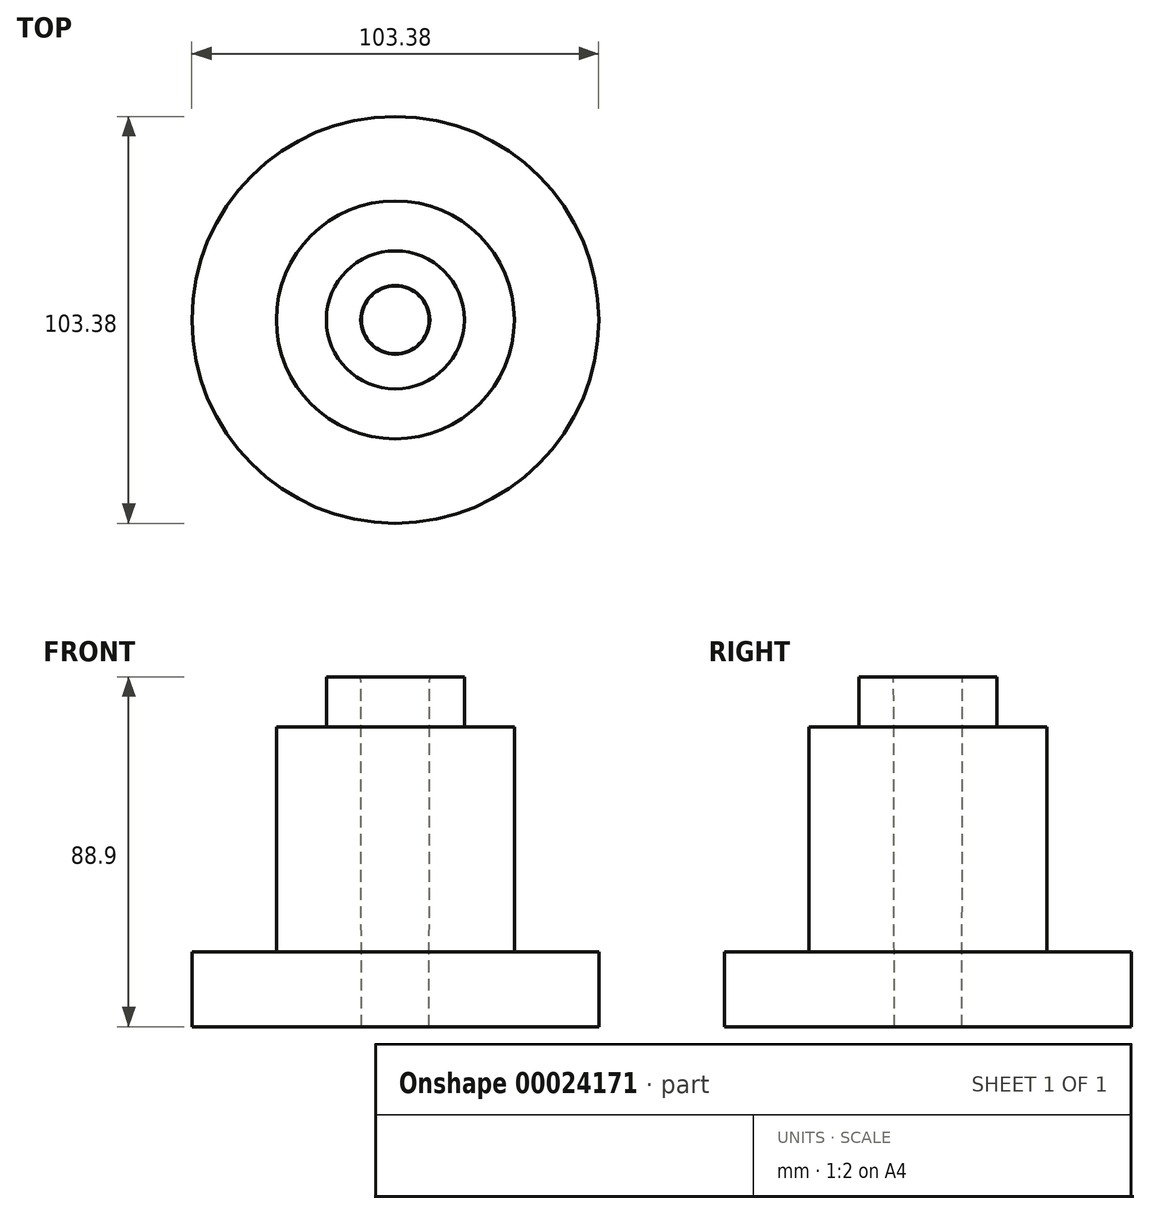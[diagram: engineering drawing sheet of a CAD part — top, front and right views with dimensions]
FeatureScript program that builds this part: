
annotation { "Feature Type Name" : "Feature", "Feature Type Description" : "" }
export const myFeature = defineFeature(function(context is Context, id is Id, definition is map)
    precondition{}
    {
        {
            var Q0;
            Q0=qCreatedBy(makeId("Front.planeOp"),FACE);
            var sketch = newSketch(context, id + "F0", { "sketchPlane" : qUnion([Q0])});
            skLineSegment(sketch, "E0", {"start": v(-616.86, 50.55) * mm, "end": v(-616.86, 37.85) * mm});
            skLineSegment(sketch, "E1", {"start": v(-616.86, 37.85) * mm, "end": v(-604.16, 37.85) * mm});
            skLineSegment(sketch, "E2", {"start": v(-604.16, 37.85) * mm, "end": v(-604.16, -19.3) * mm});
            skLineSegment(sketch, "E3", {"start": v(-604.16, -19.3) * mm, "end": v(-582.7, -19.3) * mm});
            skLineSegment(sketch, "E4", {"start": v(-582.7, -19.3) * mm, "end": v(-582.7, -38.35) * mm});
            skLineSegment(sketch, "E5", {"start": v(-616.86, 50.55) * mm, "end": v(-625.62, 50.55) * mm});
            skLineSegment(sketch, "E6", {"start": v(-582.7, -38.35) * mm, "end": v(-625.8, -38.35) * mm});
            skLineSegment(sketch, "E7", {"start": v(-625.62, 50.55) * mm, "end": v(-625.8, -38.35) * mm});
            skLineSegment(sketch, "E8", {"start": v(-634.39, 65.3) * mm, "end": v(-634.39, -40.51) * mm});
            skSolve(sketch);
        }
        {
            var Q0;
            Q0=makeQuery(id+"F0.imprint","IMPRINT",FACE,{"disambiguationData":[TD([[makeQuery(id+"F0.imprint","IMPRINT",EDGE,{"derivedFrom":sQuery(id+"F0.wireOp",EDGE,"E0")}),-1.0]])]});
            var Q1;
            Q1=sQuery(id+"F0.wireOp",EDGE,"E8");
            revolve(context, id + "F1", {"entities" : qUnion([Q0]), "axis" : qUnion([Q1]), "revolveType" : RevolveType.FULL});
        }
    });
